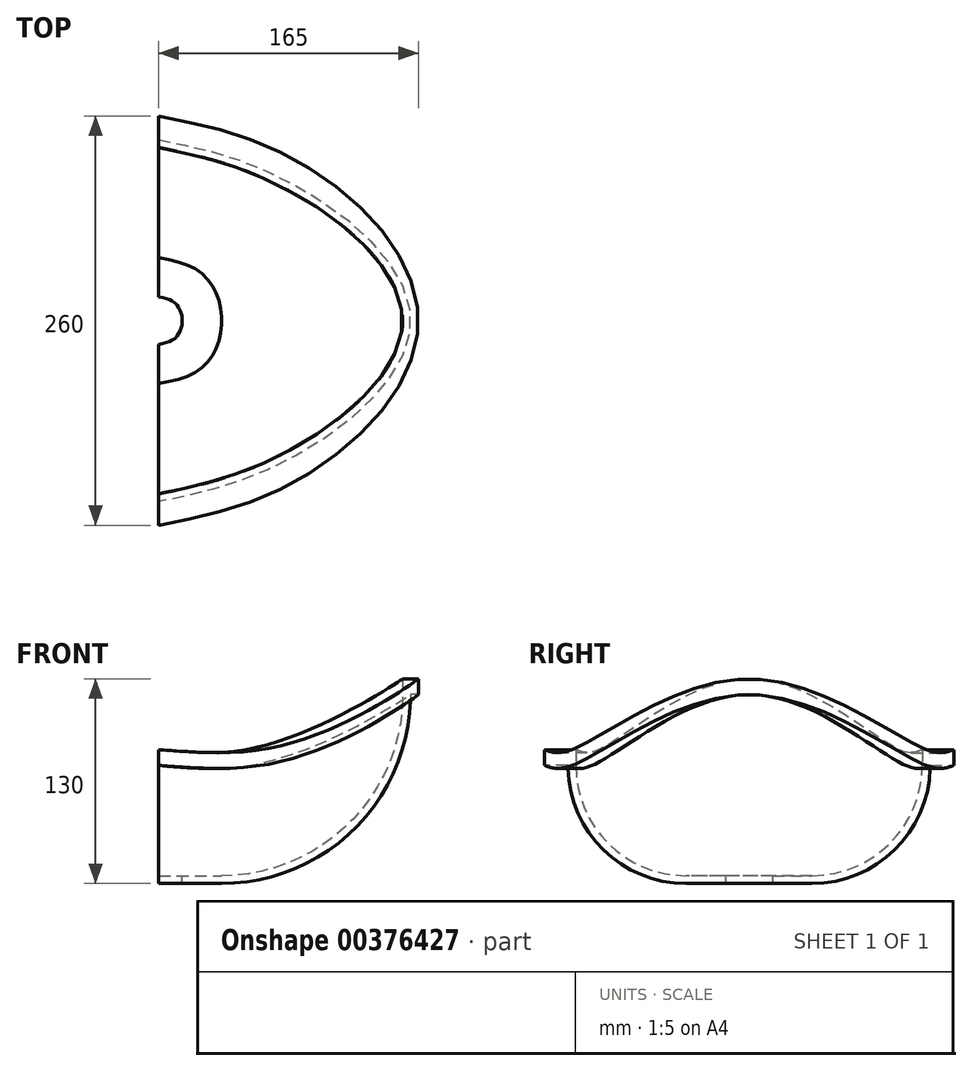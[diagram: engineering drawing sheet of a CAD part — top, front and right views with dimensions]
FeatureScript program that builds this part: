
annotation { "Feature Type Name" : "Feature", "Feature Type Description" : "" }
export const myFeature = defineFeature(function(context is Context, id is Id, definition is map)
    precondition{}
    {
        {
            var Q0;
            Q0=qCreatedBy(makeId("Front.planeOp"),FACE);
            var sketch = newSketch(context, id + "F0", { "sketchPlane" : qUnion([Q0])});
            skLineSegment(sketch, "E0.bottom", {"start": v(15, 5) * mm, "end": v(40, 5) * mm});
            skLineSegment(sketch, "E0.top", {"start": v(15, 0) * mm, "end": v(40, 0) * mm});
            skLineSegment(sketch, "E0.left", {"start": v(15, 5) * mm, "end": v(15, 0) * mm});
            skLineSegment(sketch, "E1.bottom", {"start": v(155, 130) * mm, "end": v(165, 130) * mm});
            skLineSegment(sketch, "E1.top", {"start": v(160, 120) * mm, "end": v(165, 120) * mm});
            skLineSegment(sketch, "E1.left", {"start": v(155, 130) * mm, "end": v(155, 120) * mm});
            skLineSegment(sketch, "E1.right", {"start": v(165, 130) * mm, "end": v(165, 120) * mm});
            skArc(sketch, "E2", {"start": v(40, 5) * mm, "mid": v(121.32, 38.68) * mm, "end": v(155, 120) * mm});
            skArc(sketch, "E3", {"start": v(40, 0) * mm, "mid": v(124.85, 35.15) * mm, "end": v(160, 120) * mm});
            skLineSegment(sketch, "E4", {"start": v(0, 0) * mm, "end": v(0, 227.82) * mm, "construction": true});
            skSolve(sketch);
        }
        {
            var Q0;
            Q0=sQuery(id+"F0.wireOp",EDGE,"E4");
            cPlane(context, id + "F1", {"entities" : qUnion([Q0]), "cplaneType" : CPlaneType.LINE_ANGLE, "offset" : 25 * mm, "angle" : 30 * degree, "oppositeDirection" : true, "width" : 150 * mm, "height" : 150 * mm});
        }
        {
            var Q0;
            Q0=qCreatedBy(id+"F1.planeOp",FACE);
            var sketch = newSketch(context, id + "F2", { "sketchPlane" : qUnion([Q0])});
            skLineSegment(sketch, "E5.bottom", {"start": v(15, 5) * mm, "end": v(40, 5) * mm});
            skLineSegment(sketch, "E5.top", {"start": v(15, 0) * mm, "end": v(40, 0) * mm});
            skLineSegment(sketch, "E5.left", {"start": v(15, 5) * mm, "end": v(15, 0) * mm});
            skLineSegment(sketch, "E6.bottom", {"start": v(110, 85) * mm, "end": v(130, 85) * mm});
            skLineSegment(sketch, "E6.top", {"start": v(115, 75) * mm, "end": v(130, 75) * mm});
            skLineSegment(sketch, "E6.left", {"start": v(110, 85) * mm, "end": v(110, 75) * mm});
            skLineSegment(sketch, "E6.right", {"start": v(130, 85) * mm, "end": v(130, 75) * mm});
            skArc(sketch, "E7", {"start": v(40, 5) * mm, "mid": v(89.5, 25.5) * mm, "end": v(110, 75) * mm});
            skArc(sketch, "E8", {"start": v(40, 0) * mm, "mid": v(93.03, 21.97) * mm, "end": v(115, 75) * mm});
            skLineSegment(sketch, "E9", {"start": v(0, 0) * mm, "end": v(0, 132.45) * mm, "construction": true});
            skSolve(sketch);
        }
        {
            var Q0;
            Q0=sQuery(id+"F0.wireOp",EDGE,"E4");
            cPlane(context, id + "F3", {"entities" : qUnion([Q0]), "cplaneType" : CPlaneType.LINE_ANGLE, "offset" : 25 * mm, "angle" : 150 * degree, "oppositeDirection" : true, "width" : 150 * mm, "height" : 150 * mm});
        }
        {
            var Q0;
            Q0=qCreatedBy(id+"F3.planeOp",FACE);
            var sketch = newSketch(context, id + "F4", { "sketchPlane" : qUnion([Q0])});
            skLineSegment(sketch, "E10.bottom", {"start": v(15, 5) * mm, "end": v(40, 5) * mm});
            skLineSegment(sketch, "E10.top", {"start": v(15, 0) * mm, "end": v(40, 0) * mm});
            skLineSegment(sketch, "E10.left", {"start": v(15, 5) * mm, "end": v(15, 0) * mm});
            skLineSegment(sketch, "E11.bottom", {"start": v(110, 85) * mm, "end": v(130, 85) * mm});
            skLineSegment(sketch, "E11.top", {"start": v(115, 75) * mm, "end": v(130, 75) * mm});
            skLineSegment(sketch, "E11.left", {"start": v(110, 85) * mm, "end": v(110, 75) * mm});
            skLineSegment(sketch, "E11.right", {"start": v(130, 85) * mm, "end": v(130, 75) * mm});
            skArc(sketch, "E12", {"start": v(40, 5) * mm, "mid": v(89.5, 25.5) * mm, "end": v(110, 75) * mm});
            skArc(sketch, "E13", {"start": v(40, 0) * mm, "mid": v(93.03, 21.97) * mm, "end": v(115, 75) * mm});
            skLineSegment(sketch, "E14", {"start": v(0, 0) * mm, "end": v(0, 132.45) * mm, "construction": true});
            skSolve(sketch);
        }
        {
            var Q0;
            Q0=qCreatedBy(makeId("Right.planeOp"),FACE);
            var sketch = newSketch(context, id + "F5", { "sketchPlane" : qUnion([Q0])});
            skLineSegment(sketch, "E15.bottom", {"start": v(15, 5) * mm, "end": v(40, 5) * mm});
            skLineSegment(sketch, "E15.top", {"start": v(15, 0) * mm, "end": v(40, 0) * mm});
            skLineSegment(sketch, "E15.left", {"start": v(15, 5) * mm, "end": v(15, 0) * mm});
            skLineSegment(sketch, "E16.bottom", {"start": v(110, 85) * mm, "end": v(130, 85) * mm});
            skLineSegment(sketch, "E16.top", {"start": v(115, 75) * mm, "end": v(130, 75) * mm});
            skLineSegment(sketch, "E16.left", {"start": v(110, 85) * mm, "end": v(110, 75) * mm});
            skLineSegment(sketch, "E16.right", {"start": v(130, 85) * mm, "end": v(130, 75) * mm});
            skArc(sketch, "E17", {"start": v(40, 5) * mm, "mid": v(89.5, 25.5) * mm, "end": v(110, 75) * mm});
            skArc(sketch, "E18", {"start": v(40, 0) * mm, "mid": v(93.03, 21.97) * mm, "end": v(115, 75) * mm});
            skLineSegment(sketch, "E19", {"start": v(0, 0) * mm, "end": v(0, 132.45) * mm, "construction": true});
            skLineSegment(sketch, "E20.MirrorCS", {"start": v(-15, 5) * mm, "end": v(-40, 5) * mm});
            skLineSegment(sketch, "E21.MirrorCS", {"start": v(-15, 5) * mm, "end": v(-15, 0) * mm});
            skLineSegment(sketch, "E22.MirrorCS", {"start": v(-15, 0) * mm, "end": v(-40, 0) * mm});
            skArc(sketch, "E23.MirrorCS", {"start": v(-40, 5) * mm, "mid": v(-89.5, 25.5) * mm, "end": v(-110, 75) * mm});
            skArc(sketch, "E24.MirrorCS", {"start": v(-40, 0) * mm, "mid": v(-93.03, 21.97) * mm, "end": v(-115, 75) * mm});
            skLineSegment(sketch, "E25.MirrorCS", {"start": v(-130, 85) * mm, "end": v(-130, 75) * mm});
            skLineSegment(sketch, "E26.MirrorCS", {"start": v(-110, 85) * mm, "end": v(-130, 85) * mm});
            skLineSegment(sketch, "E27.MirrorCS", {"start": v(-115, 75) * mm, "end": v(-130, 75) * mm});
            skLineSegment(sketch, "E28.MirrorCS", {"start": v(-110, 85) * mm, "end": v(-110, 75) * mm});
            skSolve(sketch);
        }
        {
            var Q0;
            Q0=makeQuery(id+"F5.imprint","IMPRINT",FACE,{"disambiguationData":[TD([[makeQuery(id+"F5.imprint","IMPRINT",EDGE,{"derivedFrom":sQuery(id+"F5.wireOp",EDGE,"E15.bottom")}),-1.0]])]});
            var Q1;
            Q1=makeQuery(id+"F2.imprint","IMPRINT",FACE,{"disambiguationData":[TD([[makeQuery(id+"F2.imprint","IMPRINT",EDGE,{"derivedFrom":sQuery(id+"F2.wireOp",EDGE,"E5.bottom")}),-1.0]])]});
            var Q2;
            Q2=makeQuery(id+"F0.imprint","IMPRINT",FACE,{"disambiguationData":[TD([[makeQuery(id+"F0.imprint","IMPRINT",EDGE,{"derivedFrom":sQuery(id+"F0.wireOp",EDGE,"E0.bottom")}),-1.0]])]});
            var Q3;
            Q3=makeQuery(id+"F4.imprint","IMPRINT",FACE,{"disambiguationData":[TD([[makeQuery(id+"F4.imprint","IMPRINT",EDGE,{"derivedFrom":sQuery(id+"F4.wireOp",EDGE,"E10.bottom")}),-1.0]])]});
            var Q4;
            Q4=makeQuery(id+"F5.imprint","IMPRINT",FACE,{"disambiguationData":[TD([[makeQuery(id+"F5.imprint","IMPRINT",EDGE,{"derivedFrom":sQuery(id+"F5.wireOp",EDGE,"E20.MirrorCS")}),1.0]])]});
            loft(context, id + "F6", {"sheetProfilesArray" : [{ "sheetProfileEntities" : qUnion([Q0]) }, { "sheetProfileEntities" : qUnion([Q1]) }, { "sheetProfileEntities" : qUnion([Q2]) }, { "sheetProfileEntities" : qUnion([Q3]) }, { "sheetProfileEntities" : qUnion([Q4]) }]});
        }
    });
